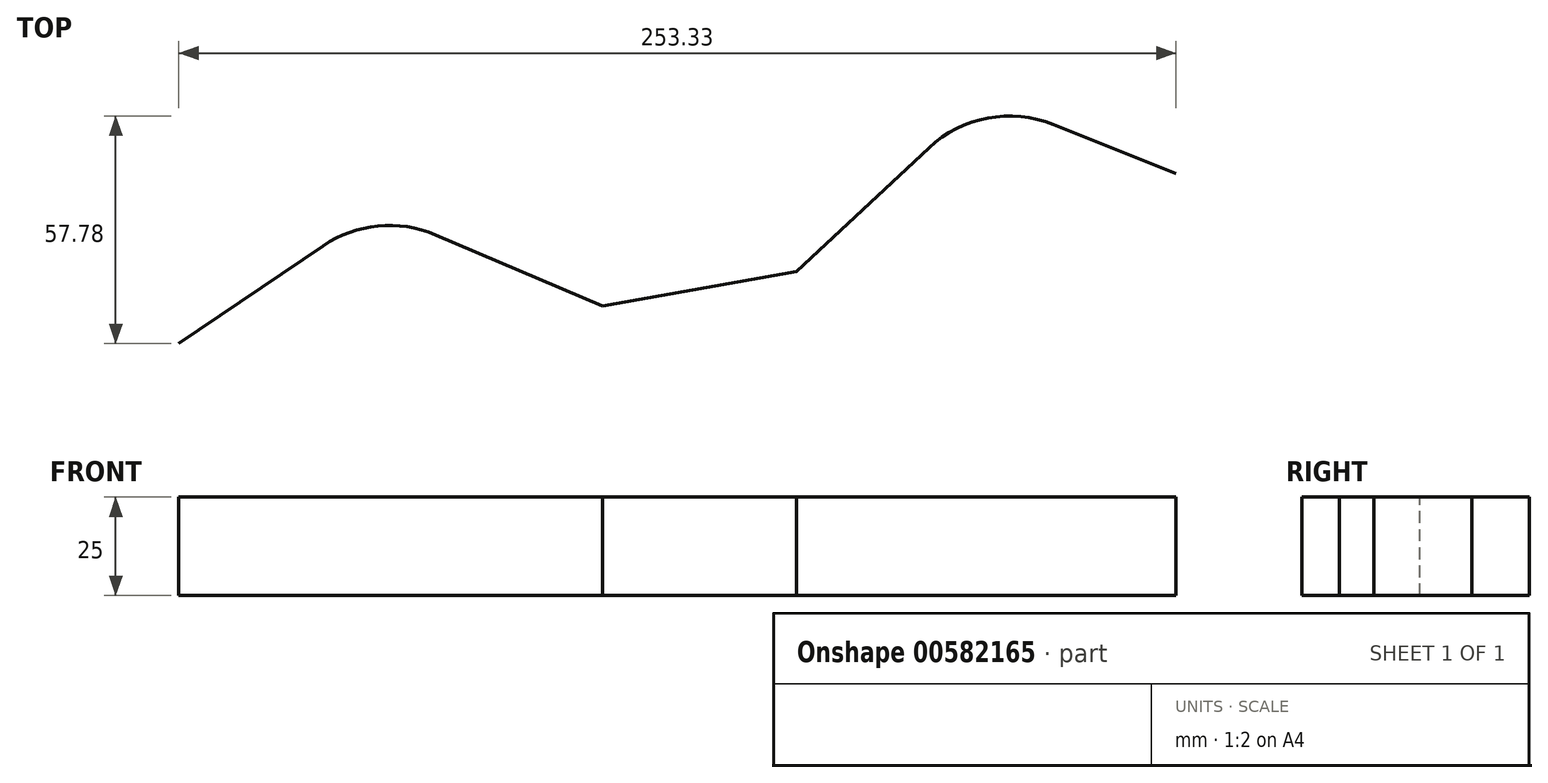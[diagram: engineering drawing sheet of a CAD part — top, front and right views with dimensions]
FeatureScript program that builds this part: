
annotation { "Feature Type Name" : "Feature", "Feature Type Description" : "" }
export const myFeature = defineFeature(function(context is Context, id is Id, definition is map)
    precondition{}
    {
        {
            var Q0;
            Q0=qCreatedBy(makeId("Top.planeOp"),FACE);
            var sketch = newSketch(context, id + "F0", { "sketchPlane" : qUnion([Q0])});
            skPoint(sketch, "E0", {"position": v(0, 0) * mm});
            skCircle(sketch, "E1", {"center": v(53.47, 0) * mm, "radius": 45 * mm, "construction": true});
            skLineSegment(sketch, "E2", {"start": v(0, 0) * mm, "end": v(53.47, 0) * mm, "construction": true});
            skLineSegment(sketch, "E3", {"start": v(0, 0) * mm, "end": v(98.47, 0) * mm, "construction": true});
            skCircle(sketch, "E4", {"center": v(211.04, 27.78) * mm, "radius": 45 * mm, "construction": true});
            skLineSegment(sketch, "E5", {"start": v(53.47, 0) * mm, "end": v(211.04, 27.78) * mm, "construction": true});
            skLineSegment(sketch, "E6", {"start": v(211.04, 27.78) * mm, "end": v(255.36, 35.6) * mm, "construction": true});
            skLineSegment(sketch, "E7", {"start": v(211.04, 27.78) * mm, "end": v(410.25, 100.3) * mm, "construction": true});
            skLineSegment(sketch, "E8", {"start": v(0, 0) * mm, "end": v(36.64, 24.83) * mm});
            skPoint(sketch, "E9", {"position": v(253.33, 43.17) * mm});
            skLineSegment(sketch, "E10", {"start": v(237.48, 13.61) * mm, "end": v(253.33, 43.17) * mm});
            skPoint(sketch, "E11", {"position": v(107.64, 9.55) * mm});
            skPoint(sketch, "E12", {"position": v(156.88, 18.23) * mm});
            skLineSegment(sketch, "E13", {"start": v(65.22, 27.6) * mm, "end": v(107.64, 9.55) * mm});
            skLineSegment(sketch, "E14", {"start": v(0, 0) * mm, "end": v(36.64, -24.83) * mm});
            skLineSegment(sketch, "E15", {"start": v(73.95, -21.92) * mm, "end": v(107.64, 9.55) * mm});
            skLineSegment(sketch, "E16", {"start": v(222.19, 55.64) * mm, "end": v(253.33, 43.17) * mm});
            skLineSegment(sketch, "E17", {"start": v(107.64, 9.55) * mm, "end": v(156.88, 18.23) * mm});
            skLineSegment(sketch, "E18", {"start": v(156.88, 18.23) * mm, "end": v(190.56, 49.7) * mm});
            skLineSegment(sketch, "E19", {"start": v(156.88, 18.23) * mm, "end": v(199.3, 0.18) * mm});
            skPoint(sketch, "E20", {"position": v(36.64, 24.83) * mm});
            skPoint(sketch, "E21", {"position": v(65.22, 27.6) * mm});
            skArc(sketch, "E22", {"start": v(36.64, 24.83) * mm, "mid": v(23.47, 0) * mm, "end": v(36.64, -24.83) * mm, "construction": true});
            skArc(sketch, "E23", {"start": v(65.22, 27.6) * mm, "mid": v(50.58, 29.86) * mm, "end": v(36.64, 24.83) * mm});
            skPoint(sketch, "E24", {"position": v(36.64, -24.83) * mm});
            skPoint(sketch, "E25", {"position": v(73.95, -21.92) * mm});
            skArc(sketch, "E26", {"start": v(73.95, -21.92) * mm, "mid": v(83.01, 5.2) * mm, "end": v(65.22, 27.6) * mm, "construction": true});
            skArc(sketch, "E27", {"start": v(36.64, -24.83) * mm, "mid": v(55.8, -29.9) * mm, "end": v(73.95, -21.92) * mm});
            skPoint(sketch, "E28", {"position": v(222.19, 55.64) * mm});
            skPoint(sketch, "E29", {"position": v(190.56, 49.7) * mm});
            skPoint(sketch, "E30", {"position": v(199.3, 0.18) * mm});
            skPoint(sketch, "E31", {"position": v(237.48, 13.61) * mm});
            skArc(sketch, "E32", {"start": v(190.56, 49.7) * mm, "mid": v(181.5, 22.57) * mm, "end": v(199.3, 0.18) * mm, "construction": true});
            skArc(sketch, "E33", {"start": v(222.19, 55.64) * mm, "mid": v(205.5, 57.27) * mm, "end": v(190.56, 49.7) * mm});
            skArc(sketch, "E34", {"start": v(199.3, 0.18) * mm, "mid": v(221, -0.52) * mm, "end": v(237.48, 13.61) * mm});
            skArc(sketch, "E35", {"start": v(237.48, 13.61) * mm, "mid": v(239.23, 38.04) * mm, "end": v(222.19, 55.64) * mm, "construction": true});
            skLineSegment(sketch, "E36", {"start": v(53.47, 0) * mm, "end": v(36.64, 24.83) * mm, "construction": true});
            skLineSegment(sketch, "E37", {"start": v(65.22, 27.6) * mm, "end": v(53.47, 0) * mm, "construction": true});
            skSolve(sketch);
        }
        {
            var Q0;
            Q0=sQuery(id+"F0.wireOp",EDGE,"E8");
            var Q1;
            Q1=sQuery(id+"F0.wireOp",EDGE,"E23");
            var Q2;
            Q2=sQuery(id+"F0.wireOp",EDGE,"E13");
            var Q3;
            Q3=sQuery(id+"F0.wireOp",EDGE,"E17");
            var Q4;
            Q4=sQuery(id+"F0.wireOp",EDGE,"E18");
            var Q5;
            Q5=sQuery(id+"F0.wireOp",EDGE,"E33");
            var Q6;
            Q6=sQuery(id+"F0.wireOp",EDGE,"E16");
            extrude(context, id + "F1", {"bodyType" : ToolBodyType.SURFACE, "surfaceEntities" : qUnion([Q0, Q1, Q2, Q3, Q4, Q5, Q6]), "depth" : 25 * mm, "offsetDistance" : 25 * mm});
        }
    });
